# Revit family: IS_ConnectBlue_Multiproduct_BIM_DE_B9933;B9934
name_source: partatom
category: Plumbing Fixtures
revit_build: Autodesk Revit MEP 2014 (Build: 20130308_1515(x64)
units: mm (PartAtom-declared; Revit-internal decimal feet)

## types (2) — shared parameters
Accessories = www.idealstandard.de\ersatzteile
AreaUnits = millimeters
Assembly Code = C1030200
AssetType = Fixed
Brand = Ideal Standard
Category = SanitaryTerminal_FAUCET
CodePerformance = EN 817, DIN 4109
Color = Chrome
ConnectionType = Plumbing
Default Elevation = 800 mm  [stored 2.62467 ft]
DurationUnit = year
ExpectedLife = 25
FaucetFunction = MIXED
FaucetOperation = LEVERHANDLE
FaucetType = PILLAR
Finish = chrome
IfcExportAs = IfcValveType
IfcExportType = FAUCET
InstallationInstructions = www.idealstandard.de/produkte
LinearUnits = millimeters
ManufacturerURL = www.idealstandard.de
Material = Brass
NBSDescription = Water supply fittings for wash basins and troughs
NBSReference = 45-35-70/371
NominalHeight = 287 mm
NominalLength = 184 mm
NominalWidth = 111 mm
ProductInformation = www.idealstandard.de/produkte
Shape = Sculptured
Size = 215x405x90mm
Space = Internal
SpareParts = www.idealstandard.de/ersatzteile
TMV3 = Yes
TestPressure = 10 Bar
URL = www.idealstandard.com
Uniclass2015Code = Pr_40_20_87_98
Uniclass2015Title = Washbasin taps
Uniclass2015Version = Products v1.1
Version = 1
VolumeUnits = Litres
WarrantyDescription = Manufacturers Warranty
WarrantyDurationUnit = year
WorkingPressure = 1-5 Bar
zero-valued in all types: CWFU, Cost, HWFU, WFU

## per-type parameters (varying)
| type | BIMObjectName | BarCode | Description | Features | FlowRate | Model | ModelNumber | ModelReference | Name | NettWeight |
| B9933AA - Connect Blue single lever basin mixer, tubular spout, no pop-up waste | ISI_IdealStandard_WashbasinTaps_ConnectBlue_B9933AA | 3800861031598 | Connect Blue single lever basin mixer, tubular spout, no pop-up waste | Connect Blue single lever basin mixer, tubular spout, no pop-up waste | 12 Liters @ 3bar | B9933AA | B9933AA | Connect Blue single lever basin mixer, tubular spout, no pop-up waste | WashbasinTaps_ConnectBlue_B9933AA_IdealStandard | 2,29 kg |
| B9934AA - Connect Blue single lever basin mixer, tubular spout, no pop-up waste, low pressure | ISI_IdealStandard_WashbasinTaps_ConnectBlue_B9934AA | 3800861031604 | Connect Blue single lever basin mixer, tubular spout, no pop-up waste, low pressure | Connect Blue single lever basin mixer, tubular spout, no pop-up waste, low pressure | 6 Liters @ 3bar | B9934AA | B9934AA | Connect Blue single lever basin mixer, tubular spout, no pop-up waste, low pressure | WashbasinTaps_ConnectBlue_B9934AA_IdealStandard | 2,38 kg |

note: [stored X ft] marks values corroborated as IEEE doubles in the binary element streams (Revit-internal decimal feet)

## geometry (parser evidence)
native form markers: Sweep x4
no freeform markers — native parametric forms only
